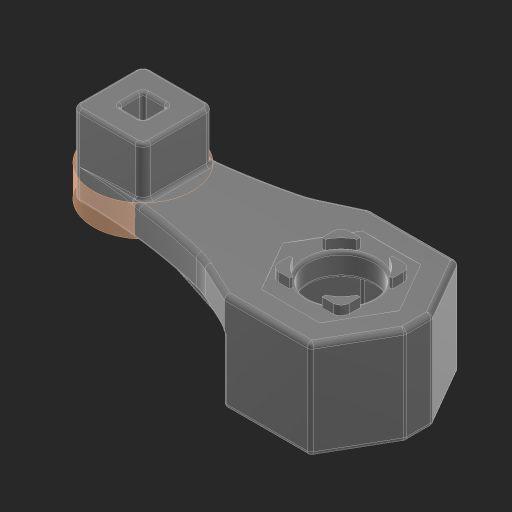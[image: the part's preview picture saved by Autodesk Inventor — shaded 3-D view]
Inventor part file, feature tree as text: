
AUTODESK INVENTOR PART (.ipt)
format: ipt  version: 2023 (Build 270158000, 158)  size: 450,560 bytes
history: native  units: in
note: dims shown in document units (in); Inventor stores cm internally (conversion verified against a paired STEP export)
features: sketch x1, projected_geometry x1, other x1, fillet x1, extrude x1
ambient origin geometry x8: Origin, YZ Plane, XZ Plane, XY Plane, X Axis, Y Axis, Z Axis, Center Point
bodies: Solid1 (feature_tree)
feature tree (5):
  sketch  "Sketch1"  dims[d1=0.3937in d2=0.0in]
  projected_geometry  "Projected Loop1"
  other  "Srf1"
  fillet  "Fillet16"  Radius=0.25in
  extrude  "ExtrusionSrf1"  [1 undecoded]
note: 1 required parameter value undecoded (feature->parameter linkage not recoverable at this tier; creation-order binding heuristic only, values carry confidence <= 0.55)
